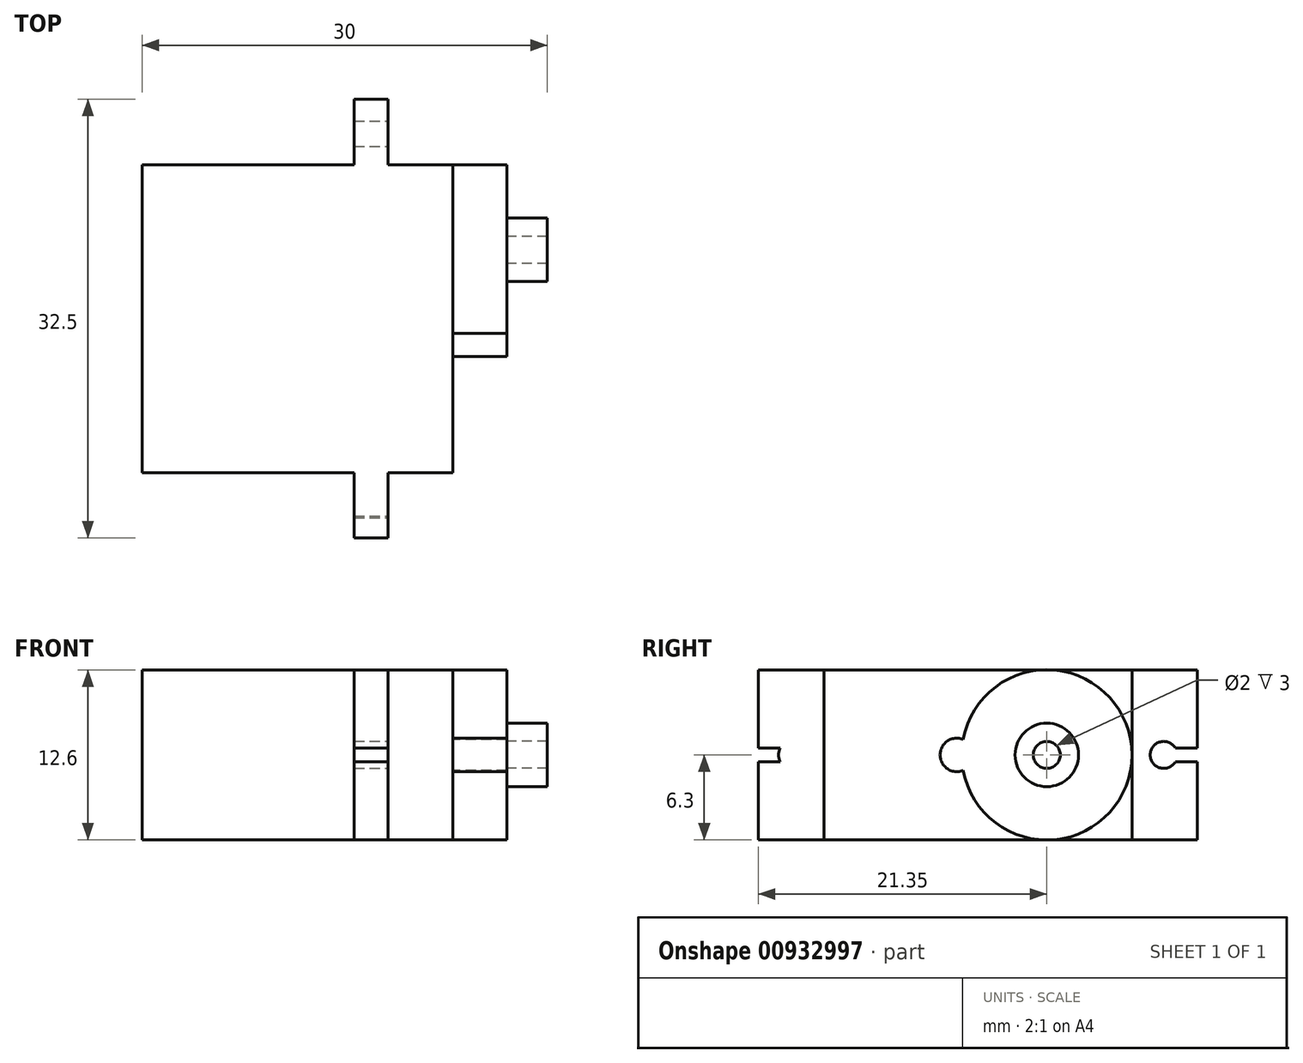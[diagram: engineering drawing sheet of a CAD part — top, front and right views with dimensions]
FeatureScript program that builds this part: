
annotation { "Feature Type Name" : "Feature", "Feature Type Description" : "" }
export const myFeature = defineFeature(function(context is Context, id is Id, definition is map)
    precondition{}
    {
        {
            var Q0;
            Q0=qCreatedBy(makeId("Top.planeOp"),FACE);
            var sketch = newSketch(context, id + "F0", { "sketchPlane" : qUnion([Q0])});
            skLineSegment(sketch, "E0", {"start": v(-8, 11.4) * mm, "end": v(-8, -11.4) * mm});
            skLineSegment(sketch, "E1", {"start": v(-8, -11.4) * mm, "end": v(7.7, -11.4) * mm});
            skLineSegment(sketch, "E2", {"start": v(7.7, -11.4) * mm, "end": v(7.7, -16.25) * mm});
            skLineSegment(sketch, "E3", {"start": v(7.7, -16.25) * mm, "end": v(10.2, -16.25) * mm});
            skLineSegment(sketch, "E4", {"start": v(10.2, -16.25) * mm, "end": v(10.2, -11.4) * mm});
            skLineSegment(sketch, "E5", {"start": v(10.2, -11.4) * mm, "end": v(15, -11.4) * mm});
            skLineSegment(sketch, "E6", {"start": v(15, -11.4) * mm, "end": v(15, 11.4) * mm});
            skLineSegment(sketch, "E7", {"start": v(15, 11.4) * mm, "end": v(10.2, 11.4) * mm});
            skLineSegment(sketch, "E8", {"start": v(10.2, 11.4) * mm, "end": v(10.2, 16.25) * mm});
            skLineSegment(sketch, "E9", {"start": v(10.2, 16.25) * mm, "end": v(7.7, 16.25) * mm});
            skLineSegment(sketch, "E10", {"start": v(7.7, 16.25) * mm, "end": v(7.7, 11.4) * mm});
            skLineSegment(sketch, "E11", {"start": v(7.7, 11.4) * mm, "end": v(-8, 11.4) * mm});
            skSolve(sketch);
        }
        {
            var Q0;
            Q0=makeQuery(id+"F0.imprint","IMPRINT",FACE,{"disambiguationData":[TD([[makeQuery(id+"F0.imprint","IMPRINT",EDGE,{"derivedFrom":sQuery(id+"F0.wireOp",EDGE,"E0")}),1.0]])]});
            extrude(context, id + "F1", {"entities" : qUnion([Q0]), "depth" : 12.6 * mm, "offsetDistance" : 25 * mm, "symmetric" : true});
        }
        {
            var Q0;
            Q0=makeQuery(id+"F1.opExtrude","SWEPT_FACE",FACE,{"disambiguationData":[OSD([sQuery(id+"F0.wireOp",EDGE,"E6")])]});
            var sketch = newSketch(context, id + "F2", { "sketchPlane" : qUnion([Q0])});
            skLineSegment(sketch, "E12", {"start": v(-11.4, 0) * mm, "end": v(11.4, 0) * mm, "construction": true});
            skCircle(sketch, "E13", {"center": v(5.1, 0) * mm, "radius": 6.3 * mm});
            skArc(sketch, "E14", {"start": v(-1.1, 1.15) * mm, "mid": v(-2.8, 0) * mm, "end": v(-1.1, -1.15) * mm});
            skSolve(sketch);
        }
        {
            var Q0;
            {var subQ0=sQuery(id+"F2.wireOp",EDGE,"E14");var subQ1=sQuery(id+"F2.wireOp",EDGE,"E13");var subQ5=makeQuery(id+"F2.imprint","INTERSECT",VERTEX,{"disambiguationData":[OD(0.0)],"derivedFrom":[subQ1,subQ0]});Q0=makeQuery(id+"F2.imprint","IMPRINT",FACE,{"disambiguationData":[TD([[makeQuery(id+"F2.imprint","IMPRINT",EDGE,{"disambiguationData":[TD([[subQ5,1.0]])],"derivedFrom":subQ1}),1.0]])]});}
            var Q1;
            {var subQ0=sQuery(id+"F2.wireOp",EDGE,"E14");Q1=makeQuery(id+"F2.imprint","IMPRINT",FACE,{"disambiguationData":[TD([[makeQuery(id+"F2.imprint","IMPRINT",EDGE,{"derivedFrom":subQ0}),1.0]])]});}
            extrude(context, id + "F3", {"entities" : qUnion([Q0, Q1]), "operationType" : NewBodyOperationType.ADD, "depth" : 4 * mm, "offsetDistance" : 25 * mm});
        }
        {
            var Q0;
            Q0=makeQuery(id+"F3.opExtrude","CAP_FACE",FACE,{"disambiguationData":[OSD([sQuery(id+"F2.wireOp",EDGE,"E13"),sQuery(id+"F2.wireOp",EDGE,"E14")])],"isStart":false});
            var sketch = newSketch(context, id + "F4", { "sketchPlane" : qUnion([Q0])});
            skCircle(sketch, "E15", {"center": v(5.1, 0) * mm, "radius": 2.35 * mm});
            skCircle(sketch, "E16", {"center": v(5.1, 0) * mm, "radius": 1 * mm});
            skSolve(sketch);
        }
        {
            var Q0;
            Q0 = qSketchRegion(id + "F4", true);
            var Q1;
            Q1=makeQuery(id+"F4.imprint","IMPRINT",FACE,{"disambiguationData":[TD([[makeQuery(id+"F4.imprint","IMPRINT",EDGE,{"derivedFrom":sQuery(id+"F4.wireOp",EDGE,"E15")}),1.0]])]});
            extrude(context, id + "F5", {"entities" : qUnion([Q0, Q1]), "operationType" : NewBodyOperationType.ADD, "depth" : 3 * mm, "offsetDistance" : 25 * mm});
        }
        {
            var Q0;
            Q0=makeQuery(id+"F1.opExtrude","SWEPT_FACE",FACE,{"disambiguationData":[OSD([sQuery(id+"F0.wireOp",EDGE,"E8")])]});
            var sketch = newSketch(context, id + "F6", { "sketchPlane" : qUnion([Q0])});
            skCircle(sketch, "E17", {"center": v(13.75, 0) * mm, "radius": 1 * mm});
            skLineSegment(sketch, "E18", {"start": v(16.25, 0) * mm, "end": v(11.4, 0) * mm, "construction": true});
            skCircle(sketch, "E19.MirrorC", {"center": v(-13.75, 0) * mm, "radius": 1 * mm});
            skLineSegment(sketch, "E20", {"start": v(14.62, 0.5) * mm, "end": v(16.25, 0.5) * mm});
            skLineSegment(sketch, "E21.MirrorCS", {"start": v(14.62, -0.5) * mm, "end": v(16.25, -0.5) * mm});
            skLineSegment(sketch, "E22", {"start": v(16.25, 0.5) * mm, "end": v(16.25, -0.5) * mm});
            skLineSegment(sketch, "E23.MirrorCS", {"start": v(-14.62, 0.5) * mm, "end": v(-16.25, 0.5) * mm});
            skLineSegment(sketch, "E24.MirrorCS", {"start": v(-14.62, -0.5) * mm, "end": v(-16.25, -0.5) * mm});
            skLineSegment(sketch, "E25.MirrorCS", {"start": v(-16.25, 0.5) * mm, "end": v(-16.25, -0.5) * mm});
            skSolve(sketch);
        }
        {
            var Q0;
            {var subQ0=sQuery(id+"F6.wireOp",EDGE,"E17");var subQ1=makeQuery(id+"F6.imprint","INTERSECT",VERTEX,{"derivedFrom":[subQ0,sQuery(id+"F6.wireOp",EDGE,"E20")]});Q0=makeQuery(id+"F6.imprint","IMPRINT",FACE,{"disambiguationData":[TD([[makeQuery(id+"F6.imprint","IMPRINT",EDGE,{"disambiguationData":[TD([[subQ1,-1.0]])],"derivedFrom":subQ0}),1.0]])]});}
            var Q1;
            {var subQ0=sQuery(id+"F6.wireOp",EDGE,"E20");Q1=makeQuery(id+"F6.imprint","IMPRINT",FACE,{"disambiguationData":[TD([[makeQuery(id+"F6.imprint","IMPRINT",EDGE,{"derivedFrom":subQ0}),-1.0]])]});}
            var Q2;
            {var subQ0=sQuery(id+"F6.wireOp",EDGE,"E19.MirrorC");var subQ1=makeQuery(id+"F6.imprint","INTERSECT",VERTEX,{"derivedFrom":[subQ0,sQuery(id+"F6.wireOp",EDGE,"E23.MirrorCS")]});Q2=makeQuery(id+"F6.imprint","IMPRINT",FACE,{"disambiguationData":[TD([[makeQuery(id+"F6.imprint","IMPRINT",EDGE,{"disambiguationData":[TD([[subQ1,-1.0]])],"derivedFrom":subQ0}),-1.0]])]});}
            var Q3;
            {var subQ0=sQuery(id+"F6.wireOp",EDGE,"E23.MirrorCS");Q3=makeQuery(id+"F6.imprint","IMPRINT",FACE,{"disambiguationData":[TD([[makeQuery(id+"F6.imprint","IMPRINT",EDGE,{"derivedFrom":subQ0}),1.0]])]});}
            extrude(context, id + "F7", {"entities" : qUnion([Q0, Q1, Q2, Q3]), "operationType" : NewBodyOperationType.REMOVE, "endBound" : BoundingType.UP_TO_NEXT, "oppositeDirection" : true, "depth" : 25 * mm, "offsetDistance" : 25 * mm});
        }
    });
